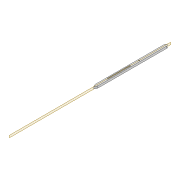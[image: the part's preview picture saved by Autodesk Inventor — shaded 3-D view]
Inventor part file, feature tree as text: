
AUTODESK INVENTOR PART (.ipt)
format: ipt  version: 2022 (Build 260153000, 153)  size: 128,512 bytes
history: native  units: mm
features: extrude x2, sketch x2, projected_geometry x1
ambient origin geometry x8: Origin, YZ Plane, XZ Plane, XY Plane, X Axis, Y Axis, Z Axis, Center Point
bodies: Solid1 (feature_tree)
feature tree (5):
  extrude  "Extrusion1"  Depth=343.336mm
  extrude  "Extrusion2"  Depth=3.0mm
  sketch  "Sketch1"  dims[d0=8.0mm d1=343.336mm]
  sketch  "Sketch3"  dims[d2=3.0mm d3=3.0mm d4=6.0mm d5=0.0mm d14=3.0mm d15=27.9mm d16=95.0mm d17=8.0mm d18=80.0mm d21=4.363323mm d22=4.363323mm d23=100.0mm d24=0.0mm]
  projected_geometry  "Projected Loop1"
